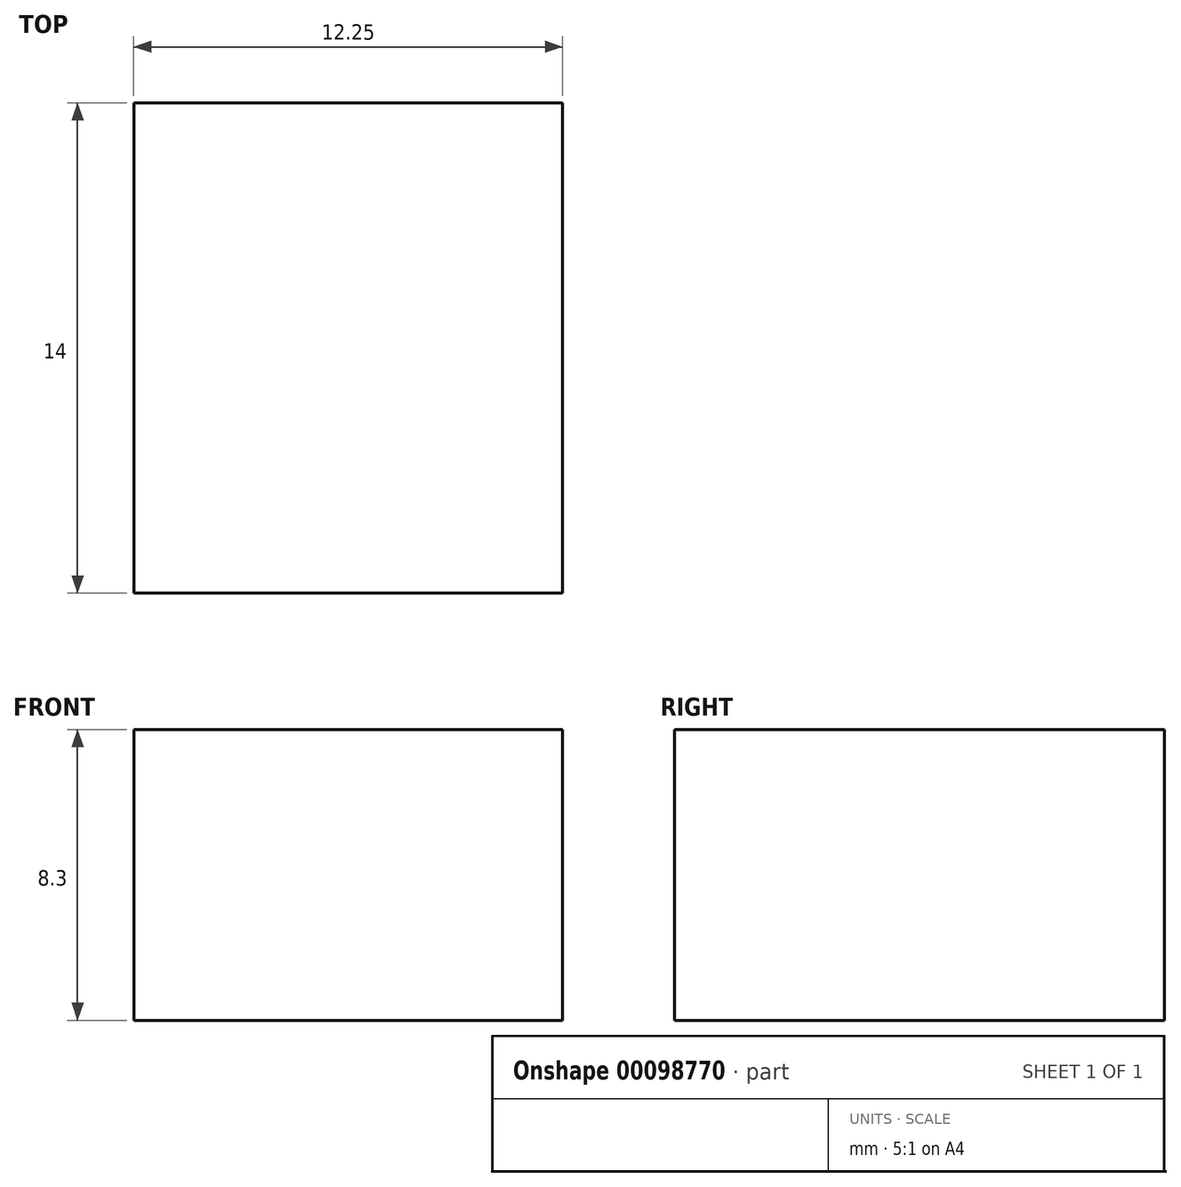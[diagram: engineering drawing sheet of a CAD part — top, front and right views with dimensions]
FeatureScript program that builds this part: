
annotation { "Feature Type Name" : "Feature", "Feature Type Description" : "" }
export const myFeature = defineFeature(function(context is Context, id is Id, definition is map)
    precondition{}
    {
        {
            var Q0;
            Q0=qCreatedBy(makeId("Top.planeOp"),FACE);
            var sketch = newSketch(context, id + "F0", { "sketchPlane" : qUnion([Q0])});
            skLineSegment(sketch, "E0", {"start": v(23.52, 0) * mm, "end": v(-22.62, 0) * mm, "construction": true});
            skLineSegment(sketch, "E1", {"start": v(2.24, 0) * mm, "end": v(2.24, -7) * mm});
            skLineSegment(sketch, "E2", {"start": v(-10, -7) * mm, "end": v(-10, 0) * mm});
            skLineSegment(sketch, "E3.MirrorCS", {"start": v(2.24, -14) * mm, "end": v(2.24, -7) * mm});
            skLineSegment(sketch, "E4.MirrorCS", {"start": v(-10, -7) * mm, "end": v(-10, -14) * mm});
            skLineSegment(sketch, "E5.MirrorCS", {"start": v(23.52, -14) * mm, "end": v(-22.62, -14) * mm, "construction": true});
            skLineSegment(sketch, "E6", {"start": v(2.24, -14) * mm, "end": v(-10, -14) * mm});
            skLineSegment(sketch, "E7", {"start": v(2.24, 0) * mm, "end": v(-10, 0) * mm});
            skSolve(sketch);
        }
        {
            var Q0;
            Q0=makeQuery(id+"F0.imprint","IMPRINT",FACE,{"disambiguationData":[TD([[makeQuery(id+"F0.imprint","IMPRINT",EDGE,{"derivedFrom":sQuery(id+"F0.wireOp",EDGE,"E1")}),-1.0]])]});
            extrude(context, id + "F1", {"entities" : qUnion([Q0]), "depth" : 8.3 * mm});
        }
    });
